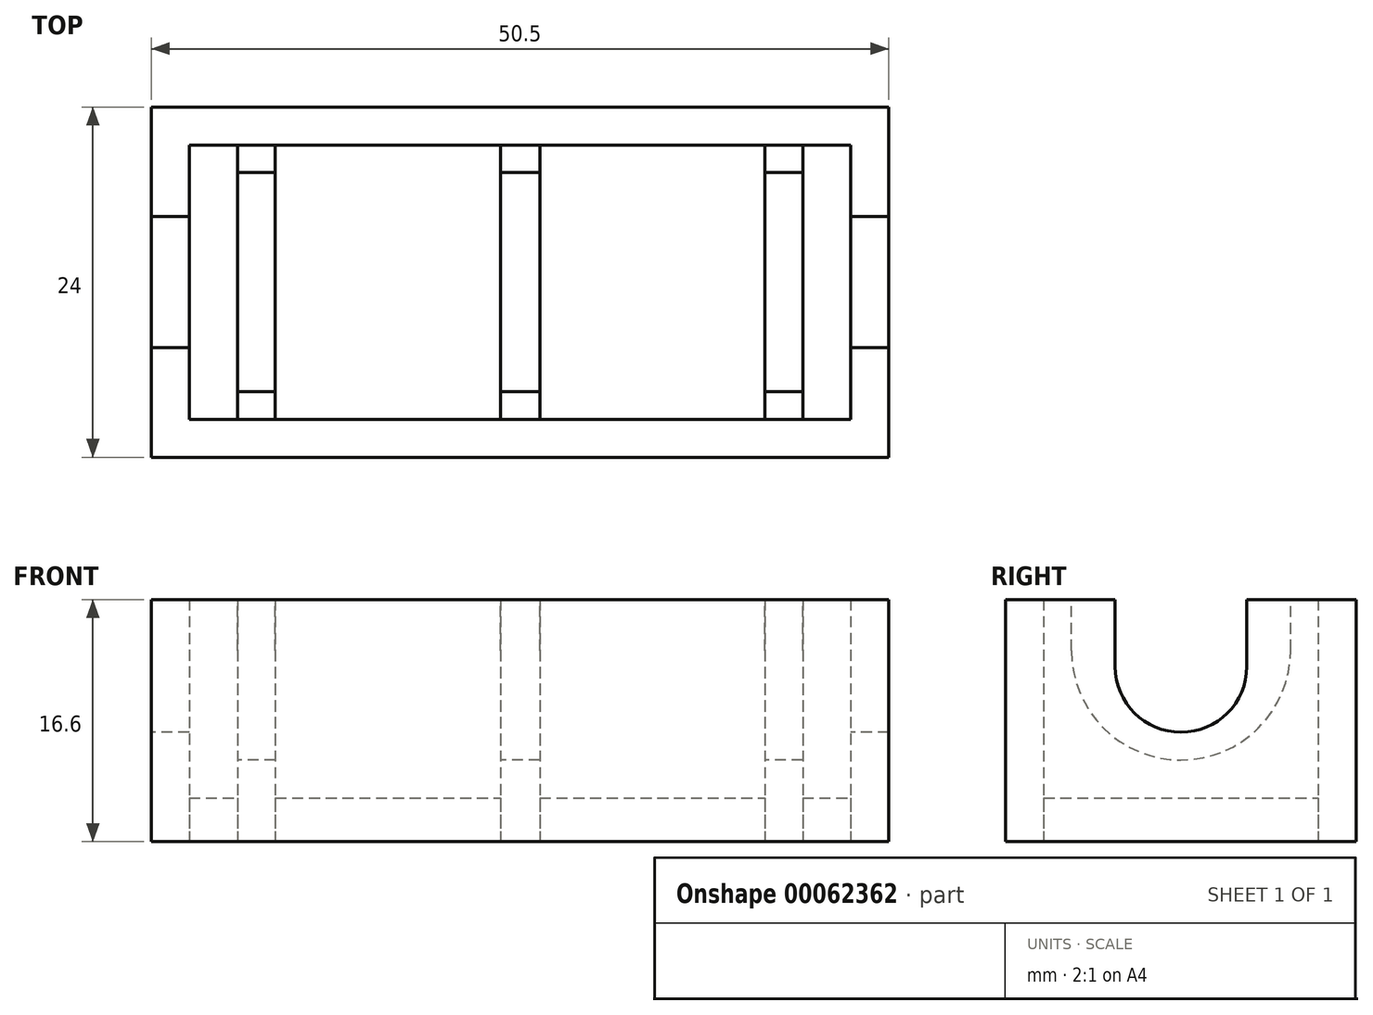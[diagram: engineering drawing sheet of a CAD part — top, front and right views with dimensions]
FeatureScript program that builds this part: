
annotation { "Feature Type Name" : "Feature", "Feature Type Description" : "" }
export const myFeature = defineFeature(function(context is Context, id is Id, definition is map)
    precondition{}
    {
        {
            var Q0;
            Q0=qCreatedBy(makeId("Top.planeOp"),FACE);
            var sketch = newSketch(context, id + "F0", { "sketchPlane" : qUnion([Q0])});
            skLineSegment(sketch, "E0.bottom", {"start": v(0, 0) * mm, "end": v(50.5, 0) * mm});
            skLineSegment(sketch, "E0.top", {"start": v(0, -69) * mm, "end": v(50.5, -69) * mm});
            skLineSegment(sketch, "E0.left", {"start": v(0, 0) * mm, "end": v(0, -69) * mm});
            skLineSegment(sketch, "E0.right", {"start": v(50.5, 0) * mm, "end": v(50.5, -69) * mm});
            skLineSegment(sketch, "E1", {"start": v(0, -45) * mm, "end": v(50.5, -45) * mm});
            skLineSegment(sketch, "E2", {"start": v(0, -24) * mm, "end": v(50.5, -24) * mm});
            skLineSegment(sketch, "E3", {"start": v(0, -24) * mm, "end": v(0, 0) * mm});
            skLineSegment(sketch, "E4", {"start": v(50.5, -24) * mm, "end": v(50.5, 0) * mm});
            skLineSegment(sketch, "E5", {"start": v(50.5, -45) * mm, "end": v(50.5, -69) * mm});
            skLineSegment(sketch, "E6", {"start": v(0, -45) * mm, "end": v(0, -69) * mm});
            skLineSegment(sketch, "E7.0", {"start": v(2.6, -21.4) * mm, "end": v(2.6, -2.6) * mm});
            skLineSegment(sketch, "E7.1", {"start": v(2.6, -21.4) * mm, "end": v(47.9, -21.4) * mm});
            skLineSegment(sketch, "E7.2", {"start": v(47.9, -21.4) * mm, "end": v(47.9, -2.6) * mm});
            skLineSegment(sketch, "E7.3", {"start": v(2.6, -2.6) * mm, "end": v(47.9, -2.6) * mm});
            skLineSegment(sketch, "E8.0", {"start": v(2.6, -47.6) * mm, "end": v(2.6, -66.4) * mm});
            skLineSegment(sketch, "E8.1", {"start": v(2.6, -47.6) * mm, "end": v(47.9, -47.6) * mm});
            skLineSegment(sketch, "E8.2", {"start": v(47.9, -47.6) * mm, "end": v(47.9, -66.4) * mm});
            skLineSegment(sketch, "E8.3", {"start": v(2.6, -66.4) * mm, "end": v(47.9, -66.4) * mm});
            skPoint(sketch, "E9", {"position": v(44.6, -66.4) * mm});
            skPoint(sketch, "E10", {"position": v(42, -66.4) * mm});
            skPoint(sketch, "E11", {"position": v(26.6, -66.4) * mm});
            skPoint(sketch, "E12", {"position": v(23.9, -66.4) * mm});
            skPoint(sketch, "E13", {"position": v(8.5, -66.4) * mm});
            skPoint(sketch, "E14", {"position": v(5.9, -66.4) * mm});
            skLineSegment(sketch, "E15", {"start": v(5.9, -66.4) * mm, "end": v(5.9, -47.6) * mm});
            skLineSegment(sketch, "E16", {"start": v(8.5, -66.4) * mm, "end": v(8.5, -47.6) * mm});
            skLineSegment(sketch, "E17", {"start": v(23.9, -66.4) * mm, "end": v(23.9, -47.6) * mm});
            skLineSegment(sketch, "E18", {"start": v(26.6, -66.4) * mm, "end": v(26.6, -47.6) * mm});
            skLineSegment(sketch, "E19", {"start": v(42, -66.4) * mm, "end": v(42, -47.6) * mm});
            skLineSegment(sketch, "E20", {"start": v(44.6, -66.4) * mm, "end": v(44.6, -47.6) * mm});
            skLineSegment(sketch, "E21", {"start": v(5.9, -21.4) * mm, "end": v(5.9, -2.6) * mm});
            skLineSegment(sketch, "E22", {"start": v(8.5, -21.4) * mm, "end": v(8.5, -2.6) * mm});
            skLineSegment(sketch, "E23", {"start": v(23.9, -21.4) * mm, "end": v(23.9, -2.6) * mm});
            skLineSegment(sketch, "E24", {"start": v(26.6, -21.4) * mm, "end": v(26.6, -2.6) * mm});
            skLineSegment(sketch, "E25", {"start": v(42, -21.4) * mm, "end": v(42, -2.6) * mm});
            skLineSegment(sketch, "E26", {"start": v(44.6, -21.4) * mm, "end": v(44.6, -2.6) * mm});
            skSolve(sketch);
        }
        {
            var Q0;
            {var subQ0=sQuery(id+"F0.wireOp",EDGE,"E8.0");Q0=makeQuery(id+"F0.imprint","IMPRINT",FACE,{"disambiguationData":[TD([[makeQuery(id+"F0.imprint","IMPRINT",EDGE,{"derivedFrom":subQ0}),1.0]])]});}
            var Q1;
            {var subQ0=sQuery(id+"F0.wireOp",EDGE,"E16");Q1=makeQuery(id+"F0.imprint","IMPRINT",FACE,{"disambiguationData":[TD([[makeQuery(id+"F0.imprint","IMPRINT",EDGE,{"derivedFrom":subQ0}),-1.0]])]});}
            var Q2;
            {var subQ0=sQuery(id+"F0.wireOp",EDGE,"E18");Q2=makeQuery(id+"F0.imprint","IMPRINT",FACE,{"disambiguationData":[TD([[makeQuery(id+"F0.imprint","IMPRINT",EDGE,{"derivedFrom":subQ0}),-1.0]])]});}
            var Q3;
            {var subQ0=sQuery(id+"F0.wireOp",EDGE,"E8.2");Q3=makeQuery(id+"F0.imprint","IMPRINT",FACE,{"disambiguationData":[TD([[makeQuery(id+"F0.imprint","IMPRINT",EDGE,{"derivedFrom":subQ0}),-1.0]])]});}
            extrude(context, id + "F1", {"entities" : qUnion([Q0, Q1, Q2, Q3]), "depth" : 3 * mm});
        }
        {
            var Q0;
            {var subQ0=sQuery(id+"F0.wireOp",EDGE,"E19");Q0=makeQuery(id+"F0.imprint","IMPRINT",FACE,{"disambiguationData":[TD([[makeQuery(id+"F0.imprint","IMPRINT",EDGE,{"derivedFrom":subQ0}),-1.0]])]});}
            var Q1;
            {var subQ0=sQuery(id+"F0.wireOp",EDGE,"E17");Q1=makeQuery(id+"F0.imprint","IMPRINT",FACE,{"disambiguationData":[TD([[makeQuery(id+"F0.imprint","IMPRINT",EDGE,{"derivedFrom":subQ0}),-1.0]])]});}
            var Q2;
            {var subQ0=sQuery(id+"F0.wireOp",EDGE,"E15");Q2=makeQuery(id+"F0.imprint","IMPRINT",FACE,{"disambiguationData":[TD([[makeQuery(id+"F0.imprint","IMPRINT",EDGE,{"derivedFrom":subQ0}),-1.0]])]});}
            extrude(context, id + "F2", {"entities" : qUnion([Q0, Q1, Q2]), "depth" : 16.6 * mm});
        }
        {
            var Q0;
            Q0=qCreatedBy(makeId("Right.planeOp"),FACE);
            var sketch = newSketch(context, id + "F3", { "sketchPlane" : qUnion([Q0])});
            skLineSegment(sketch, "E27.bottom", {"start": v(0, 0) * mm, "end": v(-69, 0) * mm});
            skLineSegment(sketch, "E27.top", {"start": v(0, 16.6) * mm, "end": v(-69, 16.6) * mm});
            skLineSegment(sketch, "E27.left", {"start": v(0, 0) * mm, "end": v(0, 16.6) * mm});
            skLineSegment(sketch, "E27.right", {"start": v(-69, 0) * mm, "end": v(-69, 16.6) * mm});
            skPoint(sketch, "E28", {"position": v(-66.4, 0) * mm});
            skPoint(sketch, "E29", {"position": v(-47.6, 0) * mm});
            skPoint(sketch, "E30", {"position": v(-2.6, 0) * mm});
            skPoint(sketch, "E31", {"position": v(-21.4, 0) * mm});
            skPoint(sketch, "E32", {"position": v(-24, 0) * mm});
            skPoint(sketch, "E33", {"position": v(-45, 0) * mm});
            skPoint(sketch, "E34", {"position": v(-57, 0) * mm});
            skLineSegment(sketch, "E35", {"start": v(-57, 0) * mm, "end": v(-57, 16.6) * mm});
            skPoint(sketch, "E36", {"position": v(-12, 0) * mm});
            skLineSegment(sketch, "E37", {"start": v(-12, 0) * mm, "end": v(-12, 16.6) * mm});
            skPoint(sketch, "E38", {"position": v(-57, 13.1) * mm});
            skCircle(sketch, "E39", {"center": v(-57, 13.1) * mm, "radius": 7.5 * mm});
            skLineSegment(sketch, "E40", {"start": v(-64.5, 13.1) * mm, "end": v(-64.5, 16.6) * mm});
            skLineSegment(sketch, "E41", {"start": v(-49.5, 13.1) * mm, "end": v(-49.5, 16.6) * mm});
            skPoint(sketch, "E42", {"position": v(-57, 12) * mm});
            skCircle(sketch, "E43", {"center": v(-57, 12) * mm, "radius": 4.5 * mm});
            skLineSegment(sketch, "E44", {"start": v(-61.5, 12) * mm, "end": v(-61.5, 16.6) * mm});
            skLineSegment(sketch, "E45", {"start": v(-52.5, 12) * mm, "end": v(-52.5, 16.6) * mm});
            skSolve(sketch);
        }
        {
            var Q0;
            {var subQ0=sQuery(id+"F3.wireOp",EDGE,"E40");Q0=makeQuery(id+"F3.imprint","IMPRINT",FACE,{"disambiguationData":[TD([[makeQuery(id+"F3.imprint","IMPRINT",EDGE,{"derivedFrom":subQ0}),-1.0]])]});}
            var Q1;
            {var subQ8=sQuery(id+"F3.wireOp",EDGE,"E44");Q1=makeQuery(id+"F3.imprint","IMPRINT",FACE,{"disambiguationData":[TD([[makeQuery(id+"F3.imprint","IMPRINT",EDGE,{"derivedFrom":subQ8}),1.0]])]});}
            var Q2;
            {var subQ4=sQuery(id+"F3.wireOp",EDGE,"E45");Q2=makeQuery(id+"F3.imprint","IMPRINT",FACE,{"disambiguationData":[TD([[makeQuery(id+"F3.imprint","IMPRINT",EDGE,{"derivedFrom":subQ4}),-1.0]])]});}
            var Q3;
            {var subQ0=sQuery(id+"F3.wireOp",EDGE,"E41");Q3=makeQuery(id+"F3.imprint","IMPRINT",FACE,{"disambiguationData":[TD([[makeQuery(id+"F3.imprint","IMPRINT",EDGE,{"derivedFrom":subQ0}),1.0]])]});}
            var Q4;
            {var subQ3=sQuery(id+"F3.wireOp",EDGE,"E44");Q4=makeQuery(id+"F3.imprint","IMPRINT",FACE,{"disambiguationData":[TD([[makeQuery(id+"F3.imprint","IMPRINT",EDGE,{"derivedFrom":subQ3}),-1.0]])]});}
            var Q5;
            {var subQ0=sQuery(id+"F3.wireOp",EDGE,"E43");var subQ1=sQuery(id+"F3.wireOp",EDGE,"E35");var subQ2=makeQuery(id+"F3.imprint","INTERSECT",VERTEX,{"disambiguationData":[OD(0.0)],"derivedFrom":[subQ1,subQ0]});Q5=makeQuery(id+"F3.imprint","IMPRINT",FACE,{"disambiguationData":[TD([[makeQuery(id+"F3.imprint","IMPRINT",EDGE,{"disambiguationData":[TD([[subQ2,-1.0]])],"derivedFrom":subQ1}),1.0]])]});}
            var Q6;
            {var subQ0=sQuery(id+"F3.wireOp",EDGE,"E43");var subQ1=sQuery(id+"F3.wireOp",EDGE,"E35");var subQ2=makeQuery(id+"F3.imprint","INTERSECT",VERTEX,{"disambiguationData":[OD(0.0)],"derivedFrom":[subQ1,subQ0]});Q6=makeQuery(id+"F3.imprint","IMPRINT",FACE,{"disambiguationData":[TD([[makeQuery(id+"F3.imprint","IMPRINT",EDGE,{"disambiguationData":[TD([[subQ2,-1.0]])],"derivedFrom":subQ1}),-1.0]])]});}
            var Q7;
            {var subQ3=sQuery(id+"F3.wireOp",EDGE,"E45");Q7=makeQuery(id+"F3.imprint","IMPRINT",FACE,{"disambiguationData":[TD([[makeQuery(id+"F3.imprint","IMPRINT",EDGE,{"derivedFrom":subQ3}),1.0]])]});}
            extrude(context, id + "F4", {"entities" : qUnion([Q0, Q1, Q2, Q3, Q4, Q5, Q6, Q7]), "operationType" : NewBodyOperationType.REMOVE, "endBound" : BoundingType.THROUGH_ALL, "depth" : 25 * mm});
        }
        {
            var Q0;
            Q0=makeQuery(id+"F0.imprint","IMPRINT",FACE,{"disambiguationData":[TD([[makeQuery(id+"F0.imprint","IMPRINT",EDGE,{"derivedFrom":sQuery(id+"F0.wireOp",EDGE,"E0.top")}),1.0]])]});
            extrude(context, id + "F5", {"entities" : qUnion([Q0]), "depth" : 16.6 * mm});
        }
        {
            var Q0;
            {var subQ3=sQuery(id+"F3.wireOp",EDGE,"E44");Q0=makeQuery(id+"F3.imprint","IMPRINT",FACE,{"disambiguationData":[TD([[makeQuery(id+"F3.imprint","IMPRINT",EDGE,{"derivedFrom":subQ3}),-1.0]])]});}
            var Q1;
            {var subQ0=sQuery(id+"F3.wireOp",EDGE,"E43");var subQ1=sQuery(id+"F3.wireOp",EDGE,"E35");var subQ2=makeQuery(id+"F3.imprint","INTERSECT",VERTEX,{"disambiguationData":[OD(0.0)],"derivedFrom":[subQ1,subQ0]});Q1=makeQuery(id+"F3.imprint","IMPRINT",FACE,{"disambiguationData":[TD([[makeQuery(id+"F3.imprint","IMPRINT",EDGE,{"disambiguationData":[TD([[subQ2,-1.0]])],"derivedFrom":subQ1}),1.0]])]});}
            var Q2;
            {var subQ0=sQuery(id+"F3.wireOp",EDGE,"E43");var subQ1=sQuery(id+"F3.wireOp",EDGE,"E35");var subQ2=makeQuery(id+"F3.imprint","INTERSECT",VERTEX,{"disambiguationData":[OD(0.0)],"derivedFrom":[subQ1,subQ0]});Q2=makeQuery(id+"F3.imprint","IMPRINT",FACE,{"disambiguationData":[TD([[makeQuery(id+"F3.imprint","IMPRINT",EDGE,{"disambiguationData":[TD([[subQ2,-1.0]])],"derivedFrom":subQ1}),-1.0]])]});}
            var Q3;
            {var subQ3=sQuery(id+"F3.wireOp",EDGE,"E45");Q3=makeQuery(id+"F3.imprint","IMPRINT",FACE,{"disambiguationData":[TD([[makeQuery(id+"F3.imprint","IMPRINT",EDGE,{"derivedFrom":subQ3}),1.0]])]});}
            extrude(context, id + "F6", {"entities" : qUnion([Q0, Q1, Q2, Q3]), "operationType" : NewBodyOperationType.REMOVE, "endBound" : BoundingType.THROUGH_ALL, "depth" : 25 * mm});
        }
    });
